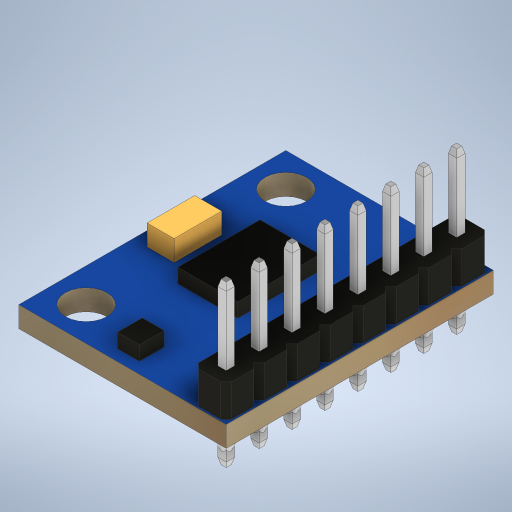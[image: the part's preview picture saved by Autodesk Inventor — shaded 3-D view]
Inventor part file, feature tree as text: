
AUTODESK INVENTOR PART (.ipt)
format: ipt  version: 2023 (Build 270158000, 158)  size: 585,728 bytes
history: native  units: mm
features: extrude x9, sketch x6, pattern_linear x1
ambient origin geometry x8: Origin, YZ Plane, XZ Plane, XY Plane, X Axis, Y Axis, Z Axis, Center Point
bodies: Solid1 (feature_tree)
feature tree (16):
  extrude  "Extrusion1"  Depth=20.6mm
  sketch  "Sketch2"  dims[d2=3.2mm d3=3.2mm]
  extrude  "Extrusion2"  Depth=3.2mm
  extrude  "Extrusion3"  Depth=2.6mm
  sketch  "Sketch3"  dims[d6=2.6mm d7=2.6mm]
  extrude  "Extrusion4"  Depth=1.6mm TaperAngle=0.0deg
  extrude  "Extrusion5"  Depth=1.912765mm
  extrude  "Extrusion6"  Depth=4.621222mm
  sketch  "Sketch5"  dims[d11=1.686216mm d12=1.912765mm]
  extrude  "Extrusion7"  Depth=2.085804mm
  extrude  "Extrusion8"  Depth=3.671807mm
  extrude  "Extrusion9"  Depth=1.09637mm
  pattern_linear  "Rectangular Pattern1"  Spacing1=1.555765mm  [1 undecoded]
  sketch  "Sketch1"  dims[d0=16.0mm d1=20.6mm]
  sketch  "Sketch4"  dims[d8=2.6mm d9=1.6mm d10=0.0mm]
  sketch  "Sketch6"  dims[d13=6.337676mm d14=4.621222mm d15=2.085804mm d16=3.671807mm d17=1.09637mm d18=1.555765mm d19=7.535914mm d20=8.806237mm d21=0.869892mm d22=6.748701mm d23=1.1mm d24=0.0mm d25=1.6mm d26=0.0mm d31=135.0deg d32=0.566mm d33=2.54mm d34=2.54mm d35=0.566mm d36=0.566mm d37=0.566mm d38=0.14mm d39=0.14mm d40=2.5mm d41=0.0mm d42=0.64mm d43=0.64mm d44=7.8mm d45=0.0mm d46=0.5mm d47=-2.443461mm d48=80.0mm d50=2.54mm d51=2.0mm d52=3.6mm d53=0.0mm d58=0.5mm d59=-2.443461mm d60=2.0mm d61=-4.363323mm d27=0.5mm d28=0.872665mm]
note: 1 required parameter value undecoded (feature->parameter linkage not recoverable at this tier; creation-order binding heuristic only, values carry confidence <= 0.55)
